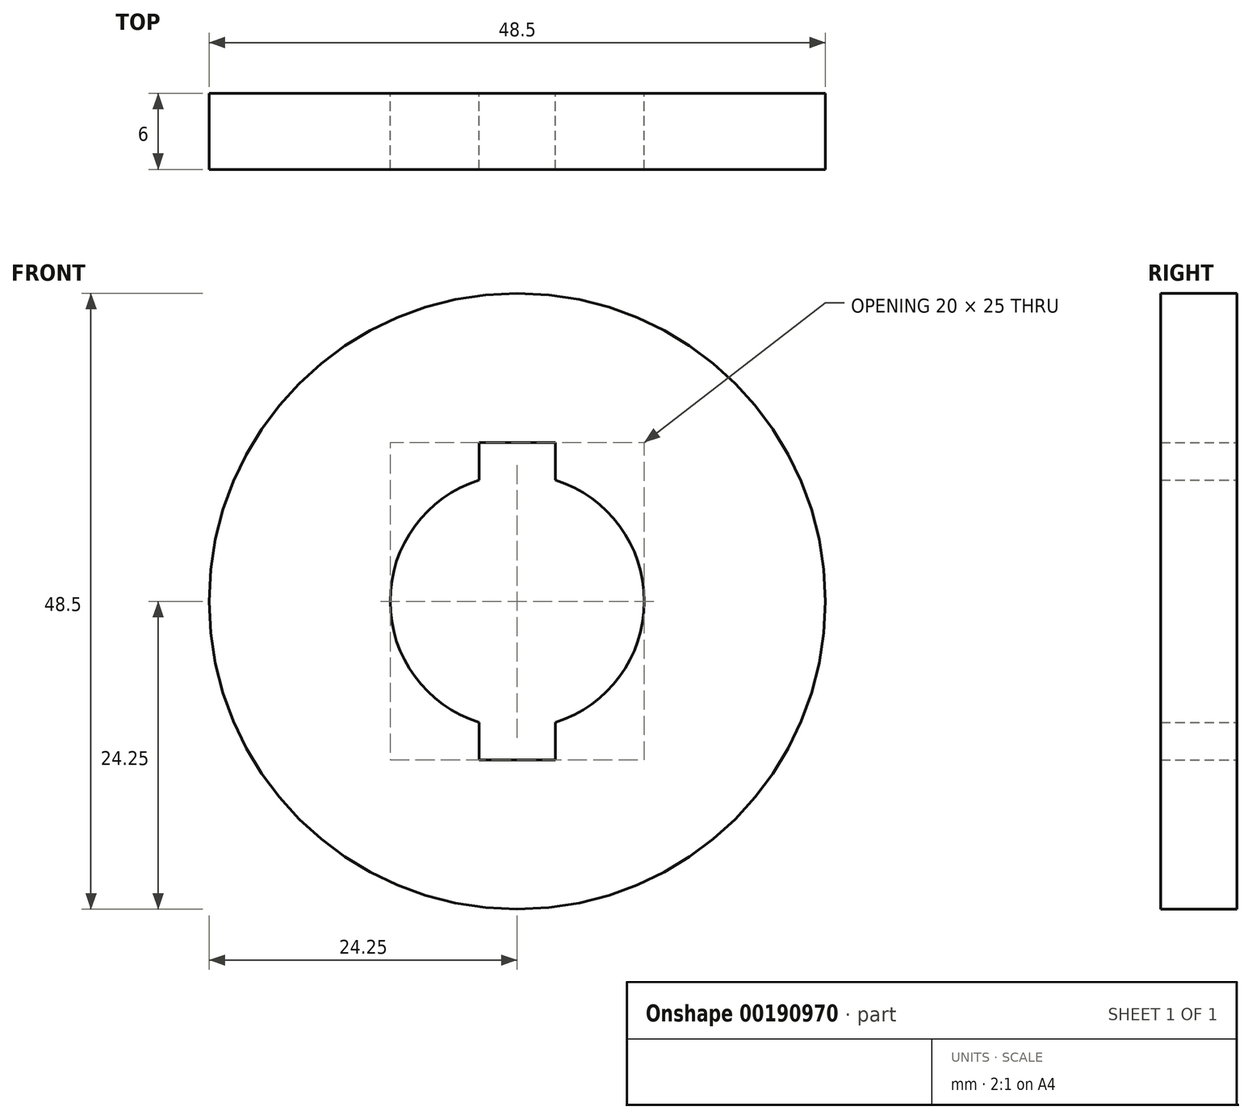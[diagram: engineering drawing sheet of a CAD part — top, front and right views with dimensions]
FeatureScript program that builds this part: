
annotation { "Feature Type Name" : "Feature", "Feature Type Description" : "" }
export const myFeature = defineFeature(function(context is Context, id is Id, definition is map)
    precondition{}
    {
        {
            var Q0;
            Q0=qCreatedBy(makeId("Front.planeOp"),FACE);
            var sketch = newSketch(context, id + "F0", { "sketchPlane" : qUnion([Q0])});
            skCircle(sketch, "E0", {"center": v(0, 0) * mm, "radius": 24.25 * mm});
            skCircle(sketch, "E1", {"center": v(0, 0) * mm, "radius": 10 * mm});
            skLineSegment(sketch, "E2.bottom", {"start": v(-3, 6.5) * mm, "end": v(3, 6.5) * mm});
            skLineSegment(sketch, "E2.top", {"start": v(-3, 12.5) * mm, "end": v(3, 12.5) * mm});
            skLineSegment(sketch, "E2.left", {"start": v(-3, 6.5) * mm, "end": v(-3, 12.5) * mm});
            skLineSegment(sketch, "E2.right", {"start": v(3, 6.5) * mm, "end": v(3, 12.5) * mm});
            skLineSegment(sketch, "E3.bottom", {"start": v(-3, -12.5) * mm, "end": v(3, -12.5) * mm});
            skLineSegment(sketch, "E3.top", {"start": v(-3, -6.5) * mm, "end": v(3, -6.5) * mm});
            skLineSegment(sketch, "E3.left", {"start": v(-3, -12.5) * mm, "end": v(-3, -6.5) * mm});
            skLineSegment(sketch, "E3.right", {"start": v(3, -12.5) * mm, "end": v(3, -6.5) * mm});
            skSolve(sketch);
        }
        {
            var Q0;
            Q0=makeQuery(id+"F0.imprint","IMPRINT",FACE,{"disambiguationData":[TD([[makeQuery(id+"F0.imprint","IMPRINT",EDGE,{"derivedFrom":sQuery(id+"F0.wireOp",EDGE,"E0")}),1.0]])]});
            extrude(context, id + "F1", {"entities" : qUnion([Q0]), "depth" : 6 * mm});
        }
    });
